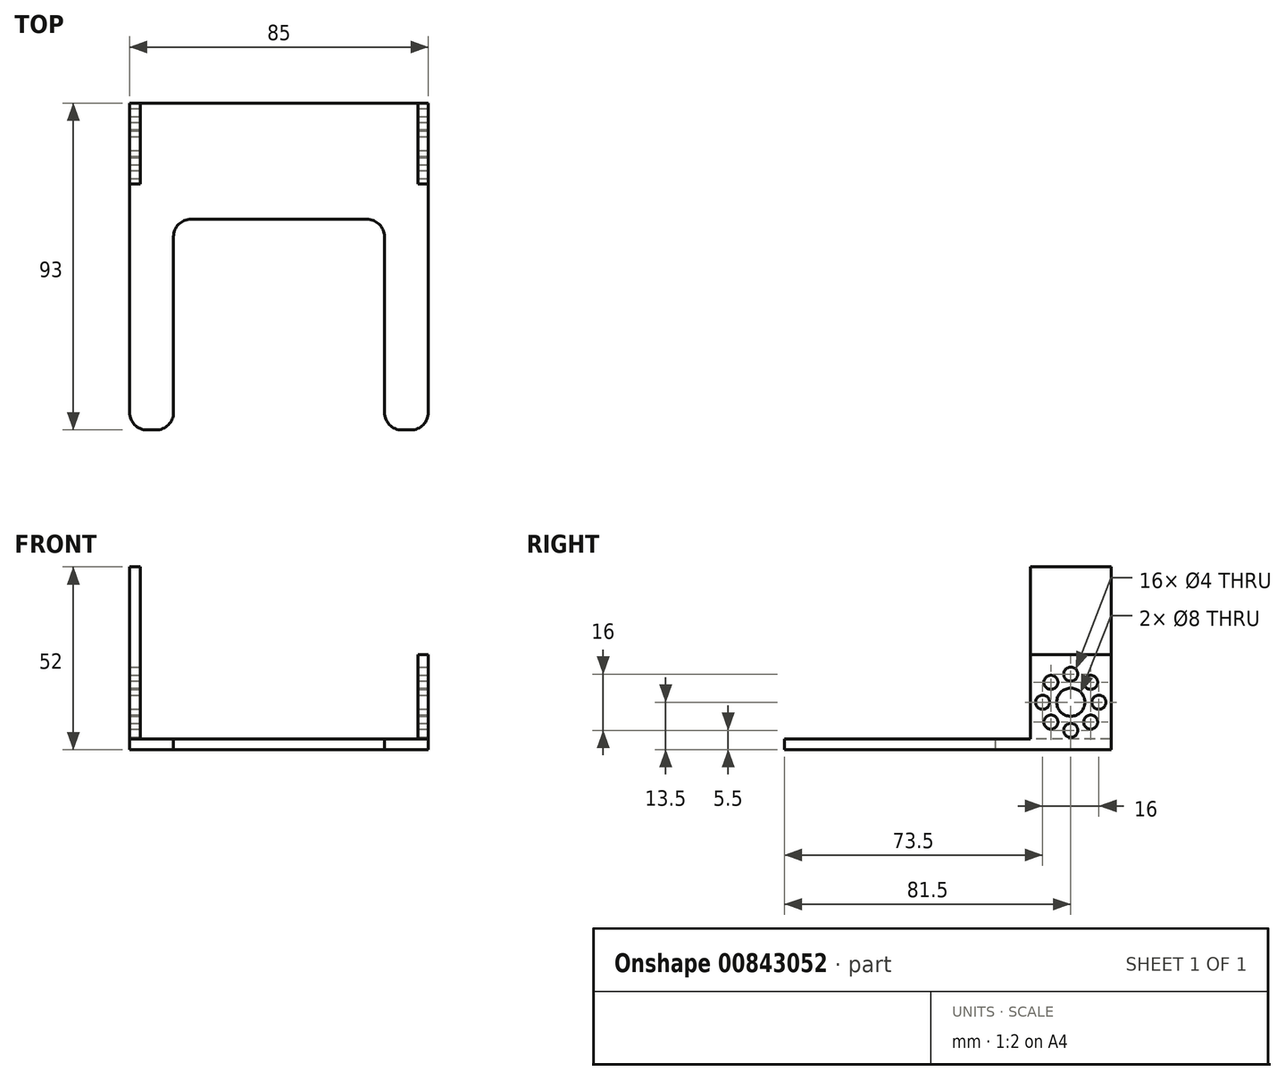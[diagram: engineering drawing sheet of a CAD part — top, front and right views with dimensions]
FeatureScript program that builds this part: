
annotation { "Feature Type Name" : "Feature", "Feature Type Description" : "" }
export const myFeature = defineFeature(function(context is Context, id is Id, definition is map)
    precondition{}
    {
        {
            var Q0;
            Q0=qCreatedBy(makeId("Top.planeOp"),FACE);
            var sketch = newSketch(context, id + "F0", { "sketchPlane" : qUnion([Q0])});
            skLineSegment(sketch, "E0.bottom", {"start": v(0, 0) * mm, "end": v(85, 0) * mm});
            skLineSegment(sketch, "E0.top", {"start": v(0, 23) * mm, "end": v(85, 23) * mm});
            skLineSegment(sketch, "E0.left", {"start": v(0, 0) * mm, "end": v(0, 23) * mm});
            skLineSegment(sketch, "E0.right", {"start": v(85, 0) * mm, "end": v(85, 23) * mm});
            skLineSegment(sketch, "E1.top", {"start": v(17.5, -10) * mm, "end": v(67.5, -10) * mm});
            skLineSegment(sketch, "E1.left", {"start": v(0, 0) * mm, "end": v(0, -10) * mm});
            skLineSegment(sketch, "E1.right", {"start": v(85, 0) * mm, "end": v(85, -10) * mm});
            skLineSegment(sketch, "E2.top", {"start": v(5, -70) * mm, "end": v(7.5, -70) * mm});
            skLineSegment(sketch, "E2.left", {"start": v(0, -10) * mm, "end": v(0, -65) * mm});
            skLineSegment(sketch, "E2.right", {"start": v(12.5, -15) * mm, "end": v(12.5, -65) * mm});
            skLineSegment(sketch, "E3.top", {"start": v(80, -70) * mm, "end": v(77.5, -70) * mm});
            skLineSegment(sketch, "E3.left", {"start": v(85, -10) * mm, "end": v(85, -65) * mm});
            skLineSegment(sketch, "E3.right", {"start": v(72.5, -15) * mm, "end": v(72.5, -65) * mm});
            skPoint(sketch, "E4.visualSharp", {"position": v(12.5, -70) * mm});
            skArc(sketch, "E4.filletArc", {"start": v(7.5, -70) * mm, "mid": v(11.04, -68.54) * mm, "end": v(12.5, -65) * mm});
            skPoint(sketch, "E5.visualSharp", {"position": v(0, -70) * mm});
            skArc(sketch, "E5.filletArc", {"start": v(0, -65) * mm, "mid": v(1.46, -68.54) * mm, "end": v(5, -70) * mm});
            skPoint(sketch, "E6.visualSharp", {"position": v(72.5, -70) * mm});
            skArc(sketch, "E6.filletArc", {"start": v(72.5, -65) * mm, "mid": v(73.96, -68.54) * mm, "end": v(77.5, -70) * mm});
            skPoint(sketch, "E7.visualSharp", {"position": v(85, -70) * mm});
            skArc(sketch, "E7.filletArc", {"start": v(80, -70) * mm, "mid": v(83.54, -68.54) * mm, "end": v(85, -65) * mm});
            skPoint(sketch, "E8.visualSharp", {"position": v(12.5, -10) * mm});
            skArc(sketch, "E8.filletArc", {"start": v(17.5, -10) * mm, "mid": v(13.96, -11.46) * mm, "end": v(12.5, -15) * mm});
            skPoint(sketch, "E9.visualSharp", {"position": v(72.5, -10) * mm});
            skArc(sketch, "E9.filletArc", {"start": v(72.5, -15) * mm, "mid": v(71.04, -11.46) * mm, "end": v(67.5, -10) * mm});
            skSolve(sketch);
        }
        {
            var Q0;
            Q0=qSketchRegion(id+"F0",true);
            extrude(context, id + "F1", {"entities" : qUnion([Q0]), "depth" : 3 * mm, "offsetDistance" : 25 * mm});
        }
        {
            var Q0;
            Q0=makeQuery(id+"F1.opExtrude","CAP_FACE",FACE,{"disambiguationData":[OSD([sQuery(id+"F0.wireOp",EDGE,"E0.bottom"),sQuery(id+"F0.wireOp",EDGE,"E0.top"),sQuery(id+"F0.wireOp",EDGE,"E0.left"),sQuery(id+"F0.wireOp",EDGE,"E0.right")])],"isStart":false});
            var sketch = newSketch(context, id + "F2", { "sketchPlane" : qUnion([Q0])});
            skLineSegment(sketch, "E10.bottom", {"start": v(0, 23) * mm, "end": v(3, 23) * mm});
            skLineSegment(sketch, "E10.top", {"start": v(0, 0) * mm, "end": v(3, 0) * mm});
            skLineSegment(sketch, "E10.left", {"start": v(0, 23) * mm, "end": v(0, 0) * mm});
            skLineSegment(sketch, "E10.right", {"start": v(3, 23) * mm, "end": v(3, 0) * mm});
            skLineSegment(sketch, "E11.bottom", {"start": v(85, 23) * mm, "end": v(82, 23) * mm});
            skLineSegment(sketch, "E11.top", {"start": v(85, 0) * mm, "end": v(82, 0) * mm});
            skLineSegment(sketch, "E11.left", {"start": v(85, 23) * mm, "end": v(85, 0) * mm});
            skLineSegment(sketch, "E11.right", {"start": v(82, 23) * mm, "end": v(82, 0) * mm});
            skSolve(sketch);
        }
        {
            var Q0;
            Q0=qSketchRegion(id+"F2",true);
            extrude(context, id + "F3", {"entities" : qUnion([Q0]), "operationType" : NewBodyOperationType.ADD, "depth" : 24 * mm, "offsetDistance" : 25 * mm});
        }
        {
            var Q0;
            Q0=makeQuery(id+"F3.opExtrude","CAP_FACE",FACE,{"disambiguationData":[OSD([sQuery(id+"F2.wireOp",EDGE,"E10.bottom"),sQuery(id+"F2.wireOp",EDGE,"E10.top"),sQuery(id+"F2.wireOp",EDGE,"E10.left"),sQuery(id+"F2.wireOp",EDGE,"E10.right")])],"isStart":false});
            var sketch = newSketch(context, id + "F4", { "sketchPlane" : qUnion([Q0])});
            skLineSegment(sketch, "E12.bottom", {"start": v(0, 23) * mm, "end": v(3, 23) * mm});
            skLineSegment(sketch, "E12.top", {"start": v(0, 0) * mm, "end": v(3, 0) * mm});
            skLineSegment(sketch, "E12.left", {"start": v(0, 23) * mm, "end": v(0, 0) * mm});
            skLineSegment(sketch, "E12.right", {"start": v(3, 23) * mm, "end": v(3, 0) * mm});
            skSolve(sketch);
        }
        {
            var Q0;
            Q0=qSketchRegion(id+"F4",true);
            extrude(context, id + "F5", {"entities" : qUnion([Q0]), "operationType" : NewBodyOperationType.ADD, "depth" : 25 * mm, "offsetDistance" : 25 * mm});
        }
        {
            var Q0;
            Q0=makeQuery(id+"F3.boolean.opBoolean","MERGE",FACE,{"derivedFrom":[makeQuery(id+"F1.opExtrude","SWEPT_FACE",FACE,{"disambiguationData":[OSD([sQuery(id+"F0.wireOp",EDGE,"E0.right"),sQuery(id+"F0.wireOp",EDGE,"E1.right"),sQuery(id+"F0.wireOp",EDGE,"E3.left")])]}),makeQuery(id+"F3.opExtrude","SWEPT_FACE",FACE,{"disambiguationData":[OSD([sQuery(id+"F2.wireOp",EDGE,"E11.left")])]})]});
            var sketch = newSketch(context, id + "F6", { "sketchPlane" : qUnion([Q0])});
            skPoint(sketch, "E13.0", {"position": v(0, 27) * mm});
            skPoint(sketch, "E14.0", {"position": v(23, 0) * mm});
            skLineSegment(sketch, "E15", {"start": v(0, 27) * mm, "end": v(23, 0) * mm, "construction": true});
            skLineSegment(sketch, "E16", {"start": v(23, 27) * mm, "end": v(0, 0) * mm, "construction": true});
            skCircle(sketch, "E17", {"center": v(19.5, 13.5) * mm, "radius": 2 * mm});
            skCircle(sketch, "E18.1.0", {"center": v(17.16, 19.16) * mm, "radius": 2 * mm});
            skCircle(sketch, "E18.2.0", {"center": v(11.5, 21.5) * mm, "radius": 2 * mm});
            skCircle(sketch, "E18.3.0", {"center": v(5.84, 19.16) * mm, "radius": 2 * mm});
            skCircle(sketch, "E18.4.0", {"center": v(3.5, 13.5) * mm, "radius": 2 * mm});
            skCircle(sketch, "E18.5.0", {"center": v(5.84, 7.84) * mm, "radius": 2 * mm});
            skCircle(sketch, "E18.6.0", {"center": v(11.5, 5.5) * mm, "radius": 2 * mm});
            skCircle(sketch, "E18.7.0", {"center": v(17.16, 7.84) * mm, "radius": 2 * mm});
            skPoint(sketch, "E18.center", {"position": v(11.5, 13.5) * mm});
            skCircle(sketch, "E19", {"center": v(11.5, 13.5) * mm, "radius": 4 * mm});
            skSolve(sketch);
        }
        {
            var Q0;
            Q0 = qSketchRegion(id + "F6", true);
            extrude(context, id + "F7", {"entities" : qUnion([Q0]), "operationType" : NewBodyOperationType.REMOVE, "oppositeDirection" : true, "depth" : 100 * mm, "offsetDistance" : 25 * mm});
        }
    });
